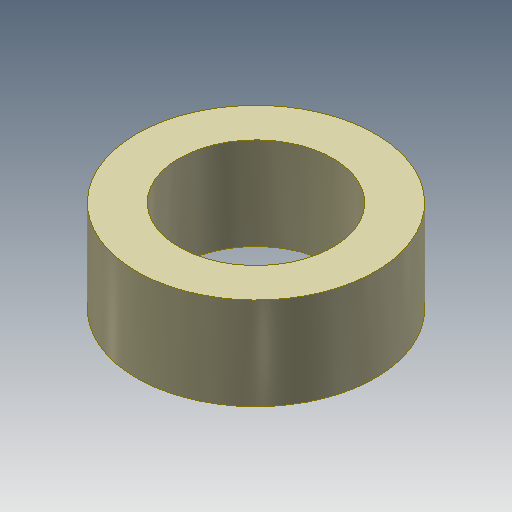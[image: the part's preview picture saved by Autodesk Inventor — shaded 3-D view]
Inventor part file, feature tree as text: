
AUTODESK INVENTOR PART (.ipt)
format: ipt  version: 2020.2 (Build 242310000, 310)  size: 95,232 bytes
history: native  units: mm
features: extrude x1, sketch x1
ambient origin geometry x8: Origin, YZ Plane, XZ Plane, XY Plane, X Axis, Y Axis, Z Axis, Center Point
bodies: Body1 (feature_tree)
feature tree (2):
  extrude  "Extrusion7"  Depth=3.0mm
  sketch  "Sketch11"  dims[d82=5.0mm d83=7.75mm d84=3.0mm d85=0.0mm]
